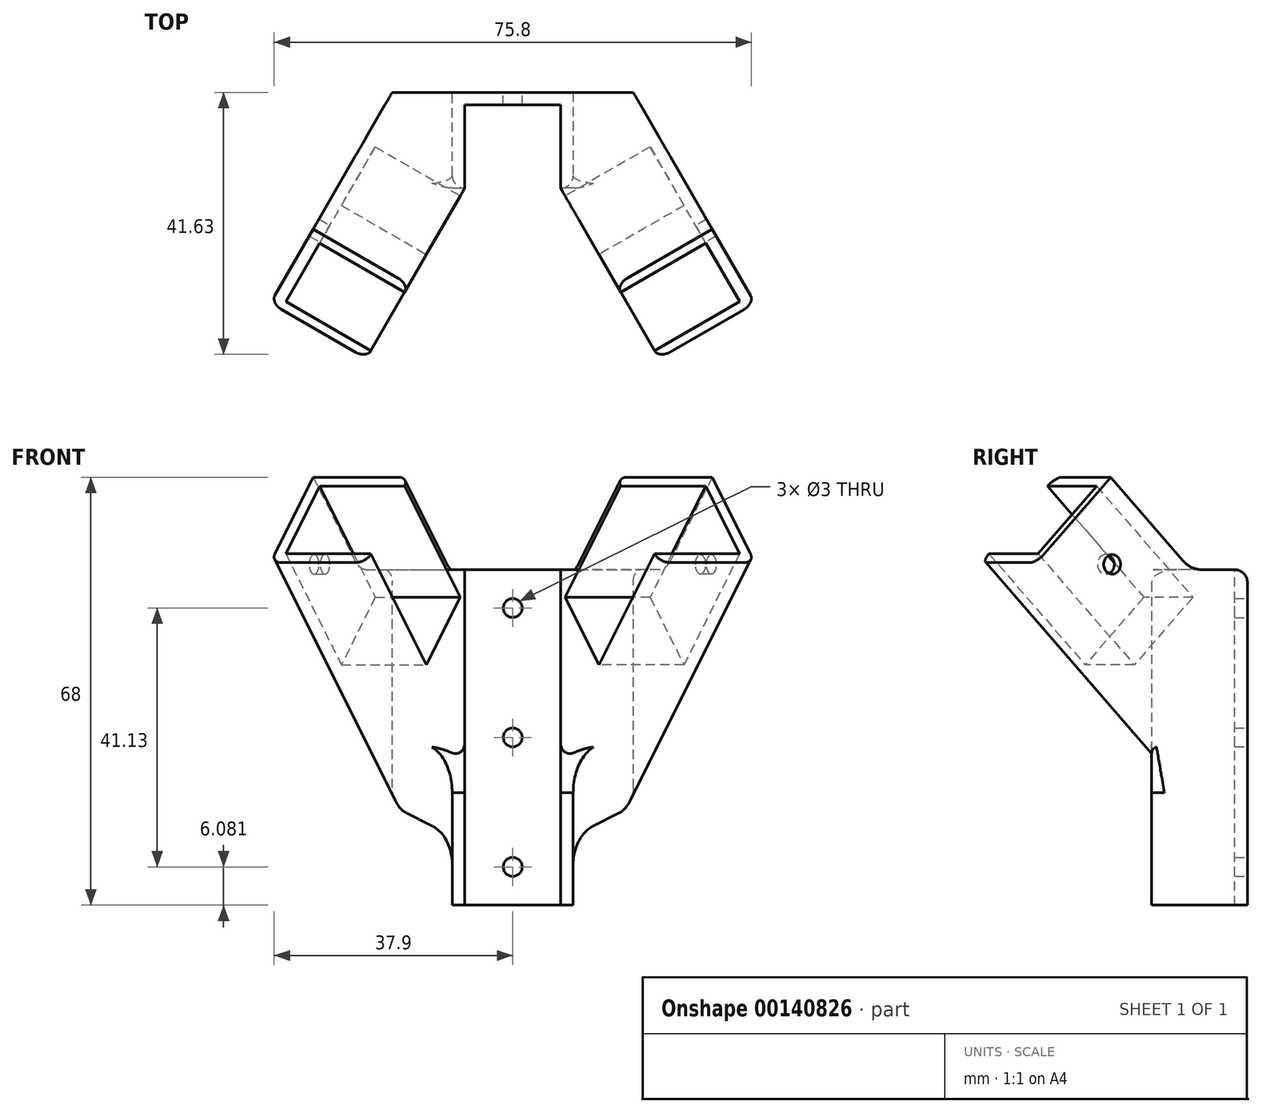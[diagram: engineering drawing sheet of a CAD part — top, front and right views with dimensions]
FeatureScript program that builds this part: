
annotation { "Feature Type Name" : "Feature", "Feature Type Description" : "" }
export const myFeature = defineFeature(function(context is Context, id is Id, definition is map)
    precondition{}
    {
        {
            var Q0;
            Q0=qCreatedBy(makeId("Top.planeOp"),FACE);
            var sketch = newSketch(context, id + "F0", { "sketchPlane" : qUnion([Q0])});
            skLineSegment(sketch, "E0", {"start": v(0, 0) * mm, "end": v(0, 0) * mm});
            skLineSegment(sketch, "E1", {"start": v(0, -15.2) * mm, "end": v(14.1, -39.62) * mm, "construction": true});
            skLineSegment(sketch, "E2", {"start": v(0, 0) * mm, "end": v(0, -15.2) * mm});
            skLineSegment(sketch, "E3", {"start": v(12.55, -7.96) * mm, "end": v(7.95, 0) * mm});
            skLineSegment(sketch, "E4", {"start": v(0, 0) * mm, "end": v(-7.6, 0) * mm});
            skLineSegment(sketch, "E5", {"start": v(-7.6, 0) * mm, "end": v(-7.6, -15.2) * mm});
            skLineSegment(sketch, "E6", {"start": v(-7.6, -15.2) * mm, "end": v(0, -15.2) * mm});
            skLineSegment(sketch, "E7", {"start": v(7.95, 0) * mm, "end": v(0, 0) * mm});
            skLineSegment(sketch, "E8", {"start": v(0, -15.2) * mm, "end": v(12.55, -7.96) * mm});
            skLineSegment(sketch, "E9", {"start": v(7.95, 0) * mm, "end": v(12.55, 0) * mm});
            skLineSegment(sketch, "E10", {"start": v(12.55, 0) * mm, "end": v(12.55, 4) * mm});
            skLineSegment(sketch, "E11", {"start": v(-7.6, 0) * mm, "end": v(-7.6, 4) * mm});
            skLineSegment(sketch, "E12", {"start": v(-7.6, 4) * mm, "end": v(12.55, 4) * mm});
            skSolve(sketch);
        }
        {
            var Q0;
            Q0=sQuery(id+"F0.wireOp",EDGE,"E1");
            var Q1;
            Q1=sQuery(id+"F0.wireOp",EDGE,"E2");
            cPlane(context, id + "F1", {"entities" : qUnion([Q0, Q1]), "cplaneType" : CPlaneType.LINE_ANGLE, "offset" : 25 * mm, "angle" : 90 * degree, "width" : 150 * mm, "height" : 150 * mm});
        }
        {
            var Q0;
            Q0=qCreatedBy(id+"F1.planeOp",FACE);
            var sketch = newSketch(context, id + "F2", { "sketchPlane" : qUnion([Q0])});
            skLineSegment(sketch, "E13", {"start": v(-16.14, 9.33) * mm, "end": v(-16.14, -15) * mm});
            skLineSegment(sketch, "E14", {"start": v(-44.42, 13.3) * mm, "end": v(-16.14, -15) * mm});
            skLineSegment(sketch, "E15", {"start": v(-30.85, 26.87) * mm, "end": v(-32.26, 25.46) * mm});
            skLineSegment(sketch, "E16", {"start": v(-32.26, 25.46) * mm, "end": v(-43, 14.7) * mm});
            skLineSegment(sketch, "E17", {"start": v(-43, 14.7) * mm, "end": v(-44.42, 13.3) * mm});
            skLineSegment(sketch, "E18", {"start": v(-30.85, 26.87) * mm, "end": v(-16.14, 12.16) * mm});
            skLineSegment(sketch, "E19", {"start": v(-16.14, 9.33) * mm, "end": v(-16.14, 12.16) * mm});
            skLineSegment(sketch, "E20", {"start": v(-18.14, 11.33) * mm, "end": v(-32.26, 25.46) * mm});
            skLineSegment(sketch, "E21", {"start": v(-43, 14.7) * mm, "end": v(-18.14, -10.16) * mm});
            skLineSegment(sketch, "E22", {"start": v(-18.14, 11.33) * mm, "end": v(-18.14, -10.16) * mm});
            skLineSegment(sketch, "E23", {"start": v(-18.14, 11.33) * mm, "end": v(-28.89, 0.59) * mm});
            skLineSegment(sketch, "E24", {"start": v(-16.14, 12.16) * mm, "end": v(-2.56, -1.41) * mm, "construction": true});
            skLineSegment(sketch, "E25", {"start": v(-16.14, -15) * mm, "end": v(-2.56, -1.41) * mm, "construction": true});
            skPoint(sketch, "E26.start.orphan", {"position": v(-3.98, 0) * mm});
            skLineSegment(sketch, "E27", {"start": v(-16.14, -15) * mm, "end": v(-3.98, -27.15) * mm});
            skLineSegment(sketch, "E28", {"start": v(-3.98, -27.15) * mm, "end": v(-3.98, 0) * mm});
            skLineSegment(sketch, "E29", {"start": v(-16.14, 12.16) * mm, "end": v(-3.98, 12.16) * mm});
            skLineSegment(sketch, "E30", {"start": v(-3.98, 12.16) * mm, "end": v(-3.98, 0) * mm});
            skLineSegment(sketch, "E31", {"start": v(-37.64, 20.08) * mm, "end": v(-23.51, 5.96) * mm, "construction": true});
            skCircle(sketch, "E32", {"center": v(-30.57, 13.02) * mm, "radius": 1.55 * mm});
            skSolve(sketch);
        }
        {
            var Q0;
            Q0=makeQuery(id+"F2.imprint","IMPRINT",FACE,{"disambiguationData":[TD([[makeQuery(id+"F2.imprint","IMPRINT",EDGE,{"derivedFrom":sQuery(id+"F2.wireOp",EDGE,"6936a970-6657-4052-9053-9d746ceb948a")}),1.0]])]});
            var Q1;
            Q1=makeQuery(id+"F2.imprint","IMPRINT",FACE,{"disambiguationData":[TD([[makeQuery(id+"F2.imprint","IMPRINT",EDGE,{"derivedFrom":sQuery(id+"F2.wireOp",EDGE,"xmnLV0OR-FJkO-aUW4-xwlg-kaku8G8oKpAe")}),1.0]])]});
            var Q2;
            {var subQ0=sQuery(id+"F2.wireOp",EDGE,"E14");Q2=makeQuery(id+"F2.imprint","IMPRINT",FACE,{"disambiguationData":[TD([[makeQuery(id+"F2.imprint","IMPRINT",EDGE,{"derivedFrom":subQ0}),1.0]])]});}
            var Q3;
            Q3=makeQuery(id+"F2.imprint","IMPRINT",FACE,{"disambiguationData":[TD([[makeQuery(id+"F2.imprint","IMPRINT",EDGE,{"derivedFrom":sQuery(id+"F2.wireOp",EDGE,"E15")}),1.0]])]});
            var Q4;
            {var subQ0=sQuery(id+"F2.wireOp",EDGE,"cLZIUdzc-nI0e-mXin-vXmg-0jIEyHkuhZyJ");Q4=makeQuery(id+"F2.imprint","IMPRINT",FACE,{"disambiguationData":[TD([[makeQuery(id+"F2.imprint","IMPRINT",EDGE,{"derivedFrom":subQ0}),1.0]])]});}
            var Q5;
            {var subQ5=sQuery(id+"F2.wireOp",EDGE,"IUePJab4-8DJg-X8FS-xd3P-ai1yPuKx8VxJ");Q5=makeQuery(id+"F2.imprint","IMPRINT",FACE,{"disambiguationData":[TD([[makeQuery(id+"F2.imprint","IMPRINT",EDGE,{"derivedFrom":subQ5}),1.0]])]});}
            var Q6;
            {var subQ5=sQuery(id+"F2.wireOp",EDGE,"E22");Q6=makeQuery(id+"F2.imprint","IMPRINT",FACE,{"disambiguationData":[TD([[makeQuery(id+"F2.imprint","IMPRINT",EDGE,{"derivedFrom":subQ5}),1.0]])]});}
            var Q7;
            {var subQ0=sQuery(id+"F2.wireOp",EDGE,"E22");Q7=makeQuery(id+"F2.imprint","IMPRINT",FACE,{"disambiguationData":[TD([[makeQuery(id+"F2.imprint","IMPRINT",EDGE,{"derivedFrom":subQ0}),-1.0]])]});}
            var Q8;
            {var subQ0=sQuery(id+"F2.wireOp",EDGE,"E16");Q8=makeQuery(id+"F2.imprint","IMPRINT",FACE,{"disambiguationData":[TD([[makeQuery(id+"F2.imprint","IMPRINT",EDGE,{"derivedFrom":subQ0}),1.0]])]});}
            var Q9;
            {var subQ1=sQuery(id+"F2.wireOp",EDGE,"E19");Q9=makeQuery(id+"F2.imprint","IMPRINT",FACE,{"disambiguationData":[TD([[makeQuery(id+"F2.imprint","IMPRINT",EDGE,{"derivedFrom":subQ1}),-1.0]])]});}
            extrude(context, id + "F3", {"entities" : qUnion([Q0, Q1, Q2, Q3, Q4, Q5, Q6, Q7, Q8, Q9]), "depth" : 17.6 * mm});
        }
        {
            var Q0;
            Q0=qCreatedBy(makeId("Top.planeOp"),FACE);
            var sketch = newSketch(context, id + "F4", { "sketchPlane" : qUnion([Q0])});
            skLineSegment(sketch, "E33", {"start": v(0, 0) * mm, "end": v(0, -15.2) * mm});
            skLineSegment(sketch, "E34", {"start": v(11.55, 1.56) * mm, "end": v(0, 1.56) * mm});
            skLineSegment(sketch, "E35", {"start": v(7.95, 0) * mm, "end": v(11.55, 0) * mm});
            skLineSegment(sketch, "E36", {"start": v(11.55, 0) * mm, "end": v(11.55, 1.56) * mm});
            skLineSegment(sketch, "E37", {"start": v(0, 1.56) * mm, "end": v(0, 0) * mm});
            skLineSegment(sketch, "E38", {"start": v(11.55, 0) * mm, "end": v(0, -15.2) * mm});
            skLineSegment(sketch, "E39", {"start": v(0, 0) * mm, "end": v(7.95, 0) * mm});
            skLineSegment(sketch, "E40", {"start": v(0, 0) * mm, "end": v(-7.63, 0) * mm});
            skLineSegment(sketch, "E41", {"start": v(-7.63, 0) * mm, "end": v(-7.63, -15.19) * mm});
            skLineSegment(sketch, "E42", {"start": v(-7.63, -15.19) * mm, "end": v(0, -15.2) * mm});
            skSolve(sketch);
        }
        {
            var Q0;
            Q0=makeQuery(id+"F3.opExtrude","CAP_FACE",FACE,{"disambiguationData":[OSD([sQuery(id+"F2.wireOp",EDGE,"E13"),sQuery(id+"F2.wireOp",EDGE,"E14"),sQuery(id+"F2.wireOp",EDGE,"E15"),sQuery(id+"F2.wireOp",EDGE,"E16"),sQuery(id+"F2.wireOp",EDGE,"E17"),sQuery(id+"F2.wireOp",EDGE,"E18"),sQuery(id+"F2.wireOp",EDGE,"E19")])],"isStart":true});
            var Q1;
            Q1=makeQuery(id+"F3.opExtrude","SWEPT_FACE",FACE,{"disambiguationData":[OSD([sQuery(id+"F2.wireOp",EDGE,"E15"),sQuery(id+"F2.wireOp",EDGE,"E16"),sQuery(id+"F2.wireOp",EDGE,"E17")])]});
            var Q2;
            Q2=makeQuery(id+"F3.opExtrude","SWEPT_FACE",FACE,{"disambiguationData":[OSD([sQuery(id+"F2.wireOp",EDGE,"E32")])]});
            shell(context, id + "F5", {"entities" : qUnion([Q0, Q1, Q2]), "thickness" : 2 * mm});
        }
        {
            var Q0;
            {var subQ0=sQuery(id+"F2.wireOp",EDGE,"E22");Q0=makeQuery(id+"F2.imprint","IMPRINT",FACE,{"disambiguationData":[TD([[makeQuery(id+"F2.imprint","IMPRINT",EDGE,{"derivedFrom":subQ0}),-1.0]])]});}
            var Q1;
            Q1=makeQuery(id+"F2.imprint","IMPRINT",FACE,{"disambiguationData":[TD([[makeQuery(id+"F2.imprint","IMPRINT",EDGE,{"derivedFrom":sQuery(id+"F2.wireOp",EDGE,"E13")}),1.0]])]});
            var Q2;
            Q2=makeQuery(id+"F2.imprint","IMPRINT",FACE,{"disambiguationData":[TD([[makeQuery(id+"F2.imprint","IMPRINT",EDGE,{"derivedFrom":sQuery(id+"F2.wireOp",EDGE,"E13")}),-1.0]])]});
            var Q3;
            Q3=makeQuery(id+"F5.opShell","OFFSET_FACE",FACE,{"disambiguationData":[OSD([sQuery(id+"F2.wireOp",EDGE,"E13"),sQuery(id+"F2.wireOp",EDGE,"E14"),sQuery(id+"F2.wireOp",EDGE,"E15"),sQuery(id+"F2.wireOp",EDGE,"E16"),sQuery(id+"F2.wireOp",EDGE,"E17"),sQuery(id+"F2.wireOp",EDGE,"E18"),sQuery(id+"F2.wireOp",EDGE,"E19")])]});
            extrude(context, id + "F6", {"entities" : qUnion([Q0, Q1, Q2]), "operationType" : NewBodyOperationType.ADD, "endBound" : BoundingType.UP_TO_SURFACE, "endBoundEntityFace" : qUnion([Q3]), "depth" : 25 * mm});
        }
        {
            var Q0;
            Q0=makeQuery(id+"F4.imprint","IMPRINT",FACE,{"disambiguationData":[TD([[makeQuery(id+"F4.imprint","IMPRINT",EDGE,{"derivedFrom":sQuery(id+"F4.wireOp",EDGE,"E33")}),1.0]])]});
            var Q1;
            Q1=makeQuery(id+"F3.opExtrude","SWEPT_FACE",FACE,{"disambiguationData":[OSD([sQuery(id+"F2.wireOp",EDGE,"E29")])]});
            var Q2;
            Q2=makeQuery(id+"F3.opExtrude","SWEPT_FACE",FACE,{"disambiguationData":[OSD([sQuery(id+"F2.wireOp",EDGE,"E14"),sQuery(id+"F2.wireOp",EDGE,"E27")])]});
            extrude(context, id + "F7", {"entities" : qUnion([Q0]), "operationType" : NewBodyOperationType.ADD, "endBound" : BoundingType.UP_TO_SURFACE, "endBoundEntityFace" : qUnion([Q1]), "depth" : 25 * mm, "hasSecondDirection" : true, "secondDirectionBound" : SecondDirectionBoundingType.UP_TO_SURFACE, "secondDirectionOppositeDirection" : true, "secondDirectionBoundEntityFace" : qUnion([Q2]), "secondDirectionDepth" : 25 * mm});
        }
        {
            var Q0;
            Q0=makeQuery(id+"F4.imprint","IMPRINT",FACE,{"disambiguationData":[TD([[makeQuery(id+"F4.imprint","IMPRINT",EDGE,{"derivedFrom":sQuery(id+"F4.wireOp",EDGE,"E34")}),1.0]])]});
            var Q1;
            {var subQ0=sQuery(id+"F2.wireOp",EDGE,"E27");var subQ1=sQuery(id+"F2.wireOp",EDGE,"E14");Q1=makeQuery(id+"F7.boolean.opBoolean","MERGE",FACE,{"derivedFrom":[makeQuery(id+"F3.opExtrude","SWEPT_FACE",FACE,{"disambiguationData":[OSD([subQ1,subQ0])]}),makeQuery(id+"F7.opExtrude","CAP_FACE",FACE,{"disambiguationData":[OSD([subQ1,subQ0])],"isStart":false})]});}
            var Q2;
            {var subQ0=sQuery(id+"F2.wireOp",EDGE,"E29");Q2=makeQuery(id+"F7.boolean.opBoolean","MERGE",FACE,{"derivedFrom":[makeQuery(id+"F3.opExtrude","SWEPT_FACE",FACE,{"disambiguationData":[OSD([subQ0])]}),makeQuery(id+"F7.opExtrude","CAP_FACE",FACE,{"disambiguationData":[OSD([subQ0])],"isStart":false})]});}
            extrude(context, id + "F8", {"entities" : qUnion([Q0]), "operationType" : NewBodyOperationType.REMOVE, "endBound" : BoundingType.UP_TO_SURFACE, "oppositeDirection" : true, "endBoundEntityFace" : qUnion([Q1]), "depth" : 25 * mm, "hasSecondDirection" : true, "secondDirectionBound" : SecondDirectionBoundingType.UP_TO_SURFACE, "secondDirectionOppositeDirection" : false, "secondDirectionBoundEntityFace" : qUnion([Q2]), "secondDirectionDepth" : 25 * mm});
        }
        {
            var Q0;
            Q0=qCreatedBy(makeId("Front.planeOp"),FACE);
            var sketch = newSketch(context, id + "F9", { "sketchPlane" : qUnion([Q0])});
            skLineSegment(sketch, "E43", {"start": v(-7.6, -41.13) * mm, "end": v(0, -41.13) * mm});
            skLineSegment(sketch, "E44", {"start": v(0, -31.13) * mm, "end": v(0, 12.16) * mm});
            skLineSegment(sketch, "E45", {"start": v(0, -31.13) * mm, "end": v(0, -41.13) * mm});
            skLineSegment(sketch, "E46", {"start": v(0, -31.13) * mm, "end": v(-7.6, -31.13) * mm});
            skLineSegment(sketch, "E47", {"start": v(-7.6, -31.13) * mm, "end": v(-7.6, 12.16) * mm});
            skLineSegment(sketch, "E48", {"start": v(-7.6, 12.16) * mm, "end": v(0, 12.16) * mm});
            skLineSegment(sketch, "E49", {"start": v(-7.6, -31.13) * mm, "end": v(-7.6, -41.13) * mm});
            skLineSegment(sketch, "E50", {"start": v(0, -41.13) * mm, "end": v(2, -41.13) * mm});
            skLineSegment(sketch, "E51", {"start": v(2, -41.13) * mm, "end": v(2, 12.16) * mm});
            skLineSegment(sketch, "E52", {"start": v(2, 12.16) * mm, "end": v(0, 12.16) * mm});
            skSolve(sketch);
        }
        {
            var Q0;
            Q0=makeQuery(id+"F9.imprint","IMPRINT",FACE,{"disambiguationData":[TD([[makeQuery(id+"F9.imprint","IMPRINT",EDGE,{"derivedFrom":sQuery(id+"F9.wireOp",EDGE,"E44")}),1.0]])]});
            var Q1;
            Q1=makeQuery(id+"F9.imprint","IMPRINT",FACE,{"disambiguationData":[TD([[makeQuery(id+"F9.imprint","IMPRINT",EDGE,{"derivedFrom":sQuery(id+"F9.wireOp",EDGE,"E44")}),-1.0]])]});
            extrude(context, id + "F10", {"entities" : qUnion([Q0, Q1]), "operationType" : NewBodyOperationType.ADD, "depth" : 15.2 * mm});
        }
        {
            var Q0;
            Q0=makeQuery(id+"F6.opExtrude","SWEPT_FACE",FACE,{"disambiguationData":[OSD([sQuery(id+"F2.wireOp",EDGE,"E23")])]});
            extrude(context, id + "F11", {"entities" : qUnion([Q0]), "operationType" : NewBodyOperationType.REMOVE, "oppositeDirection" : true, "depth" : 5 * mm});
        }
        {
            var Q0;
            Q0=makeQuery(id+"F3.opExtrude","SWEPT_BODY",BODY,{"disambiguationData":[OSD([sQuery(id+"F2.wireOp",EDGE,"E14"),sQuery(id+"F2.wireOp",EDGE,"E15"),sQuery(id+"F2.wireOp",EDGE,"E16"),sQuery(id+"F2.wireOp",EDGE,"E17"),sQuery(id+"F2.wireOp",EDGE,"E18"),sQuery(id+"F2.wireOp",EDGE,"E27"),sQuery(id+"F2.wireOp",EDGE,"E28"),sQuery(id+"F2.wireOp",EDGE,"E29"),sQuery(id+"F2.wireOp",EDGE,"E30"),sQuery(id+"F2.wireOp",EDGE,"E32")])]});
            var Q1;
            Q1=makeQuery(id+"F10.opExtrude","SWEPT_FACE",FACE,{"disambiguationData":[OSD([sQuery(id+"F9.wireOp",EDGE,"E47")])]});
            mirror(context, id + "F12", {"operationType" : NewBodyOperationType.ADD, "entities" : qUnion([Q0]), "mirrorPlane" : qUnion([Q1])});
        }
        {
            var Q0;
            {var subQ0=sQuery(id+"F2.wireOp",EDGE,"E29");var subQ1=makeQuery(id+"F10.boolean.opBoolean","MERGE",FACE,{"derivedFrom":[makeQuery(id+"F7.boolean.opBoolean","MERGE",FACE,{"derivedFrom":[makeQuery(id+"F3.opExtrude","SWEPT_FACE",FACE,{"disambiguationData":[OSD([subQ0])]}),makeQuery(id+"F7.opExtrude","CAP_FACE",FACE,{"disambiguationData":[OSD([subQ0])],"isStart":false})]}),makeQuery(id+"F10.opExtrude","SWEPT_FACE",FACE,{"disambiguationData":[OSD([sQuery(id+"F9.wireOp",EDGE,"E48")])]})]});Q0=makeQuery(id+"F12.boolean.opBoolean","MERGE",FACE,{"derivedFrom":[subQ1,makeQuery(id+"F12.opPattern","COPY",FACE,{"derivedFrom":subQ1,"instanceName":"1"})]});}
            var sketch = newSketch(context, id + "F13", { "sketchPlane" : qUnion([Q0])});
            skLineSegment(sketch, "E53", {"start": v(-15.2, -15.2) * mm, "end": v(-15.2, 0) * mm});
            skLineSegment(sketch, "E54", {"start": v(-15.2, 0) * mm, "end": v(0, 0) * mm});
            skLineSegment(sketch, "E55", {"start": v(0, 0) * mm, "end": v(0, -15.2) * mm});
            skLineSegment(sketch, "E56", {"start": v(0, -15.2) * mm, "end": v(-15.2, -15.2) * mm});
            skLineSegment(sketch, "E57", {"start": v(-15.2, -2) * mm, "end": v(0, -2) * mm});
            skSolve(sketch);
        }
        {
            var Q0;
            {var subQ0=sQuery(id+"F13.wireOp",EDGE,"E56");Q0=makeQuery(id+"F13.imprint","IMPRINT",FACE,{"disambiguationData":[TD([[makeQuery(id+"F13.imprint","IMPRINT",EDGE,{"derivedFrom":subQ0}),1.0]])]});}
            var Q1;
            Q1=makeQuery(id+"F12.opPattern","COPY",FACE,{"derivedFrom":makeQuery(id+"F10.opExtrude","SWEPT_FACE",FACE,{"disambiguationData":[OSD([sQuery(id+"F9.wireOp",EDGE,"E50")])]}),"instanceName":"1"});
            extrude(context, id + "F14", {"entities" : qUnion([Q0]), "operationType" : NewBodyOperationType.REMOVE, "endBound" : BoundingType.UP_TO_NEXT, "oppositeDirection" : true, "endBoundEntityFace" : qUnion([Q1]), "depth" : 25 * mm});
        }
        {
            var Q0;
            {var subQ0=makeQuery(id+"F10.opExtrude","SWEPT_FACE",FACE,{"disambiguationData":[OSD([sQuery(id+"F9.wireOp",EDGE,"E46")])]});Q0=makeQuery(id+"F12.boolean.opBoolean","MERGE",FACE,{"derivedFrom":[subQ0,makeQuery(id+"F12.opPattern","COPY",FACE,{"derivedFrom":subQ0,"instanceName":"1"})]});}
            var Q1;
            Q1=makeQuery(id+"F12.opPattern","COPY",FACE,{"derivedFrom":makeQuery(id+"F10.opExtrude","SWEPT_FACE",FACE,{"disambiguationData":[OSD([sQuery(id+"F9.wireOp",EDGE,"E50")])]}),"instanceName":"1"});
            extrude(context, id + "F15", {"entities" : qUnion([Q0]), "operationType" : NewBodyOperationType.ADD, "endBound" : BoundingType.UP_TO_SURFACE, "endBoundEntityFace" : qUnion([Q1]), "depth" : 25 * mm});
        }
        {
            var Q0;
            {var subQ0=sQuery(id+"F9.wireOp",EDGE,"E46");var subQ1=sQuery(id+"F4.wireOp",EDGE,"E39");var subQ2=sQuery(id+"F4.wireOp",EDGE,"E35");var subQ3=makeQuery(id+"F10.boolean.opBoolean","MERGE",FACE,{"derivedFrom":[makeQuery(id+"F8.boolean.opBoolean","MERGE",FACE,{"derivedFrom":[makeQuery(id+"F7.opExtrude","SWEPT_FACE",FACE,{"disambiguationData":[OSD([subQ2,subQ1])]}),makeQuery(id+"F8.opExtrude","SWEPT_FACE",FACE,{"disambiguationData":[OSD([subQ2,subQ1])]})]}),makeQuery(id+"F10.opExtrude","CAP_FACE",FACE,{"disambiguationData":[OSD([sQuery(id+"F9.wireOp",EDGE,"E45"),subQ0,sQuery(id+"F9.wireOp",EDGE,"E47"),sQuery(id+"F9.wireOp",EDGE,"E48"),sQuery(id+"F9.wireOp",EDGE,"E50"),sQuery(id+"F9.wireOp",EDGE,"E51"),sQuery(id+"F9.wireOp",EDGE,"E52")])],"isStart":true})]});Q0=makeQuery(id+"F15.boolean.opBoolean","MERGE",FACE,{"derivedFrom":[makeQuery(id+"F12.boolean.opBoolean","MERGE",FACE,{"derivedFrom":[subQ3,makeQuery(id+"F12.opPattern","COPY",FACE,{"derivedFrom":subQ3,"instanceName":"1"})]}),makeQuery(id+"F15.opExtrude","SWEPT_FACE",FACE,{"disambiguationData":[OSD([subQ0])]})]});}
            var sketch = newSketch(context, id + "F16", { "sketchPlane" : qUnion([Q0])});
            skLineSegment(sketch, "E58", {"start": v(7.6, 12.16) * mm, "end": v(7.6, 0) * mm, "construction": true});
            skCircle(sketch, "E59", {"center": v(7.6, 6.08) * mm, "radius": 1.55 * mm});
            skLineSegment(sketch, "E60", {"start": v(7.6, 12.16) * mm, "end": v(7.6, -41.13) * mm, "construction": true});
            skCircle(sketch, "E61", {"center": v(7.6, -14.48) * mm, "radius": 1.55 * mm});
            skCircle(sketch, "E62", {"center": v(7.6, -35.05) * mm, "radius": 1.55 * mm});
            skSolve(sketch);
        }
        {
            var Q0;
            Q0=sQuery(id+"F16.wireOp",VERTEX,"E59.center");
            var Q1;
            Q1=sQuery(id+"F16.wireOp",VERTEX,"E61.center");
            var Q2;
            Q2=sQuery(id+"F16.wireOp",VERTEX,"E62.center");
            var Q3;
            Q3=makeQuery(id+"F3.opExtrude","SWEPT_BODY",BODY,{"disambiguationData":[OSD([sQuery(id+"F2.wireOp",EDGE,"E14"),sQuery(id+"F2.wireOp",EDGE,"E15"),sQuery(id+"F2.wireOp",EDGE,"E16"),sQuery(id+"F2.wireOp",EDGE,"E17"),sQuery(id+"F2.wireOp",EDGE,"E18"),sQuery(id+"F2.wireOp",EDGE,"E27"),sQuery(id+"F2.wireOp",EDGE,"E28"),sQuery(id+"F2.wireOp",EDGE,"E29"),sQuery(id+"F2.wireOp",EDGE,"E30"),sQuery(id+"F2.wireOp",EDGE,"E32")])]});
            hole(context, id + "F17", {"style" : HoleStyle.SIMPLE, "endStyle" : HoleEndStyle.THROUGH, "holeDiameter" : 3 * mm, "locations" : qUnion([Q0, Q1, Q2]), "scope" : qUnion([Q3]), "isTappedThrough" : true});
        }
        {
            var Q0;
            Q0=makeQuery(id+"F12.opPattern","COPY",EDGE,{"derivedFrom":makeQuery(id+"F3.opExtrude","SWEPT_EDGE",EDGE,{"disambiguationData":[OSD([sQuery(id+"F2.wireOp",EDGE,"E18"),sQuery(id+"F2.wireOp",EDGE,"E19"),sQuery(id+"F2.wireOp",EDGE,"E29")])]}),"instanceName":"1"});
            var Q1;
            Q1=makeQuery(id+"F3.opExtrude","SWEPT_EDGE",EDGE,{"disambiguationData":[OSD([sQuery(id+"F2.wireOp",EDGE,"E18"),sQuery(id+"F2.wireOp",EDGE,"E19"),sQuery(id+"F2.wireOp",EDGE,"E29")])]});
            var Q2;
            {var subQ0=sQuery(id+"F2.wireOp",EDGE,"E27");var subQ1=sQuery(id+"F2.wireOp",EDGE,"E14");Q2=makeQuery(id+"F12.opPattern","COPY",EDGE,{"derivedFrom":makeQuery(id+"F10.boolean.opBoolean","INTERSECT",EDGE,{"derivedFrom":[makeQuery(id+"F7.boolean.opBoolean","MERGE",FACE,{"derivedFrom":[makeQuery(id+"F3.opExtrude","SWEPT_FACE",FACE,{"disambiguationData":[OSD([subQ1,subQ0])]}),makeQuery(id+"F7.opExtrude","CAP_FACE",FACE,{"disambiguationData":[OSD([subQ1,subQ0])],"isStart":false})]}),makeQuery(id+"F10.opExtrude","SWEPT_FACE",FACE,{"disambiguationData":[OSD([sQuery(id+"F9.wireOp",EDGE,"E51")])]})]}),"instanceName":"1"});}
            var Q3;
            {var subQ0=sQuery(id+"F2.wireOp",EDGE,"E27");var subQ1=sQuery(id+"F2.wireOp",EDGE,"E14");Q3=makeQuery(id+"F10.boolean.opBoolean","INTERSECT",EDGE,{"derivedFrom":[makeQuery(id+"F7.boolean.opBoolean","MERGE",FACE,{"derivedFrom":[makeQuery(id+"F3.opExtrude","SWEPT_FACE",FACE,{"disambiguationData":[OSD([subQ1,subQ0])]}),makeQuery(id+"F7.opExtrude","CAP_FACE",FACE,{"disambiguationData":[OSD([subQ1,subQ0])],"isStart":false})]}),makeQuery(id+"F10.opExtrude","SWEPT_FACE",FACE,{"disambiguationData":[OSD([sQuery(id+"F9.wireOp",EDGE,"E51")])]})]});}
            var Q4;
            Q4=makeQuery(id+"F8.boolean.opBoolean","COPY",EDGE,{"derivedFrom":makeQuery(id+"F8.opExtrude","TWEAK_EDGE",EDGE,{"derivedFrom":[makeQuery(id+"F4.imprint","IMPRINT",EDGE,{"derivedFrom":sQuery(id+"F4.wireOp",EDGE,"E35")}),makeQuery(id+"F4.imprint","IMPRINT",EDGE,{"derivedFrom":sQuery(id+"F4.wireOp",EDGE,"E36")}),makeQuery(id+"F4.imprint","IMPRINT",EDGE,{"derivedFrom":sQuery(id+"F4.wireOp",EDGE,"E39")})]})});
            var Q5;
            Q5=makeQuery(id+"F12.opPattern","COPY",EDGE,{"derivedFrom":makeQuery(id+"F8.boolean.opBoolean","COPY",EDGE,{"derivedFrom":makeQuery(id+"F8.opExtrude","TWEAK_EDGE",EDGE,{"derivedFrom":[makeQuery(id+"F4.imprint","IMPRINT",EDGE,{"derivedFrom":sQuery(id+"F4.wireOp",EDGE,"E35")}),makeQuery(id+"F4.imprint","IMPRINT",EDGE,{"derivedFrom":sQuery(id+"F4.wireOp",EDGE,"E36")}),makeQuery(id+"F4.imprint","IMPRINT",EDGE,{"derivedFrom":sQuery(id+"F4.wireOp",EDGE,"E39")})]})}),"instanceName":"1"});
            fillet(context, id + "F18", {"entities" : qUnion([Q0, Q1, Q2, Q3, Q4, Q5]), "radius" : 5 * mm, "tangentPropagation" : true, "allowEdgeOverflow" : false});
        }
        {
            var Q0;
            {var subQ0=sQuery(id+"F2.wireOp",EDGE,"E29");var subQ1=makeQuery(id+"F3.opExtrude","SWEPT_FACE",FACE,{"disambiguationData":[OSD([subQ0])]});var subQ2=makeQuery(id+"F4.imprint","IMPRINT",EDGE,{"derivedFrom":sQuery(id+"F4.wireOp",EDGE,"E39")});var subQ3=makeQuery(id+"F4.imprint","IMPRINT",EDGE,{"derivedFrom":sQuery(id+"F4.wireOp",EDGE,"E35")});var subQ4=makeQuery(id+"F10.boolean.opBoolean","MERGE",EDGE,{"derivedFrom":[makeQuery(id+"F8.boolean.opBoolean","MERGE",EDGE,{"derivedFrom":[makeQuery(id+"F7.opExtrude","TWEAK_EDGE",EDGE,{"derivedFrom":[subQ3,subQ2,subQ1]}),makeQuery(id+"F8.opExtrude","TWEAK_EDGE",EDGE,{"derivedFrom":[subQ3,subQ2,makeQuery(id+"F7.boolean.opBoolean","MERGE",FACE,{"derivedFrom":[subQ1,makeQuery(id+"F7.opExtrude","CAP_FACE",FACE,{"disambiguationData":[OSD([subQ0])],"isStart":false})]})]})]}),makeQuery(id+"F10.opExtrude","CAP_EDGE",EDGE,{"disambiguationData":[OSD([sQuery(id+"F9.wireOp",EDGE,"E48"),sQuery(id+"F9.wireOp",EDGE,"E52")])],"isStart":true})]});Q0=makeQuery(id+"F12.boolean.opBoolean","MERGE",EDGE,{"derivedFrom":[subQ4,makeQuery(id+"F12.opPattern","COPY",EDGE,{"derivedFrom":subQ4,"instanceName":"1"})]});}
            var Q1;
            Q1=makeQuery(id+"F3.opExtrude","CAP_EDGE",EDGE,{"disambiguationData":[OSD([sQuery(id+"F2.wireOp",EDGE,"E14"),sQuery(id+"F2.wireOp",EDGE,"E27")])],"isStart":false});
            var Q2;
            Q2=makeQuery(id+"F12.opPattern","COPY",EDGE,{"derivedFrom":makeQuery(id+"F3.opExtrude","CAP_EDGE",EDGE,{"disambiguationData":[OSD([sQuery(id+"F2.wireOp",EDGE,"E14"),sQuery(id+"F2.wireOp",EDGE,"E27")])],"isStart":false}),"instanceName":"1"});
            var Q3;
            Q3=makeQuery(id+"F10.opExtrude","CAP_EDGE",EDGE,{"disambiguationData":[OSD([sQuery(id+"F9.wireOp",EDGE,"E51")])],"isStart":false});
            var Q4;
            Q4=makeQuery(id+"F12.opPattern","COPY",EDGE,{"derivedFrom":makeQuery(id+"F10.opExtrude","CAP_EDGE",EDGE,{"disambiguationData":[OSD([sQuery(id+"F9.wireOp",EDGE,"E51")])],"isStart":false}),"instanceName":"1"});
            var Q5;
            Q5=makeQuery(id+"F3.opExtrude","CAP_EDGE",EDGE,{"disambiguationData":[OSD([sQuery(id+"F2.wireOp",EDGE,"E18")])],"isStart":true});
            var Q6;
            Q6=makeQuery(id+"F12.opPattern","COPY",EDGE,{"derivedFrom":makeQuery(id+"F3.opExtrude","CAP_EDGE",EDGE,{"disambiguationData":[OSD([sQuery(id+"F2.wireOp",EDGE,"E18")])],"isStart":true}),"instanceName":"1"});
            fillet(context, id + "F19", {"entities" : qUnion([Q0, Q1, Q2, Q3, Q4, Q5, Q6]), "radius" : 2 * mm, "tangentPropagation" : true, "allowEdgeOverflow" : false});
        }
        {
            var Q0;
            Q0=makeQuery(id+"F12.opPattern","COPY",EDGE,{"derivedFrom":makeQuery(id+"F3.opExtrude","CAP_EDGE",EDGE,{"disambiguationData":[OSD([sQuery(id+"F2.wireOp",EDGE,"E14"),sQuery(id+"F2.wireOp",EDGE,"E27")])],"isStart":true}),"instanceName":"1"});
            var Q1;
            Q1=makeQuery(id+"F3.opExtrude","CAP_EDGE",EDGE,{"disambiguationData":[OSD([sQuery(id+"F2.wireOp",EDGE,"E14"),sQuery(id+"F2.wireOp",EDGE,"E27")])],"isStart":true});
            fillet(context, id + "F20", {"entities" : qUnion([Q0, Q1]), "radius" : 2 * mm, "tangentPropagation" : true, "allowEdgeOverflow" : false});
        }
    });
